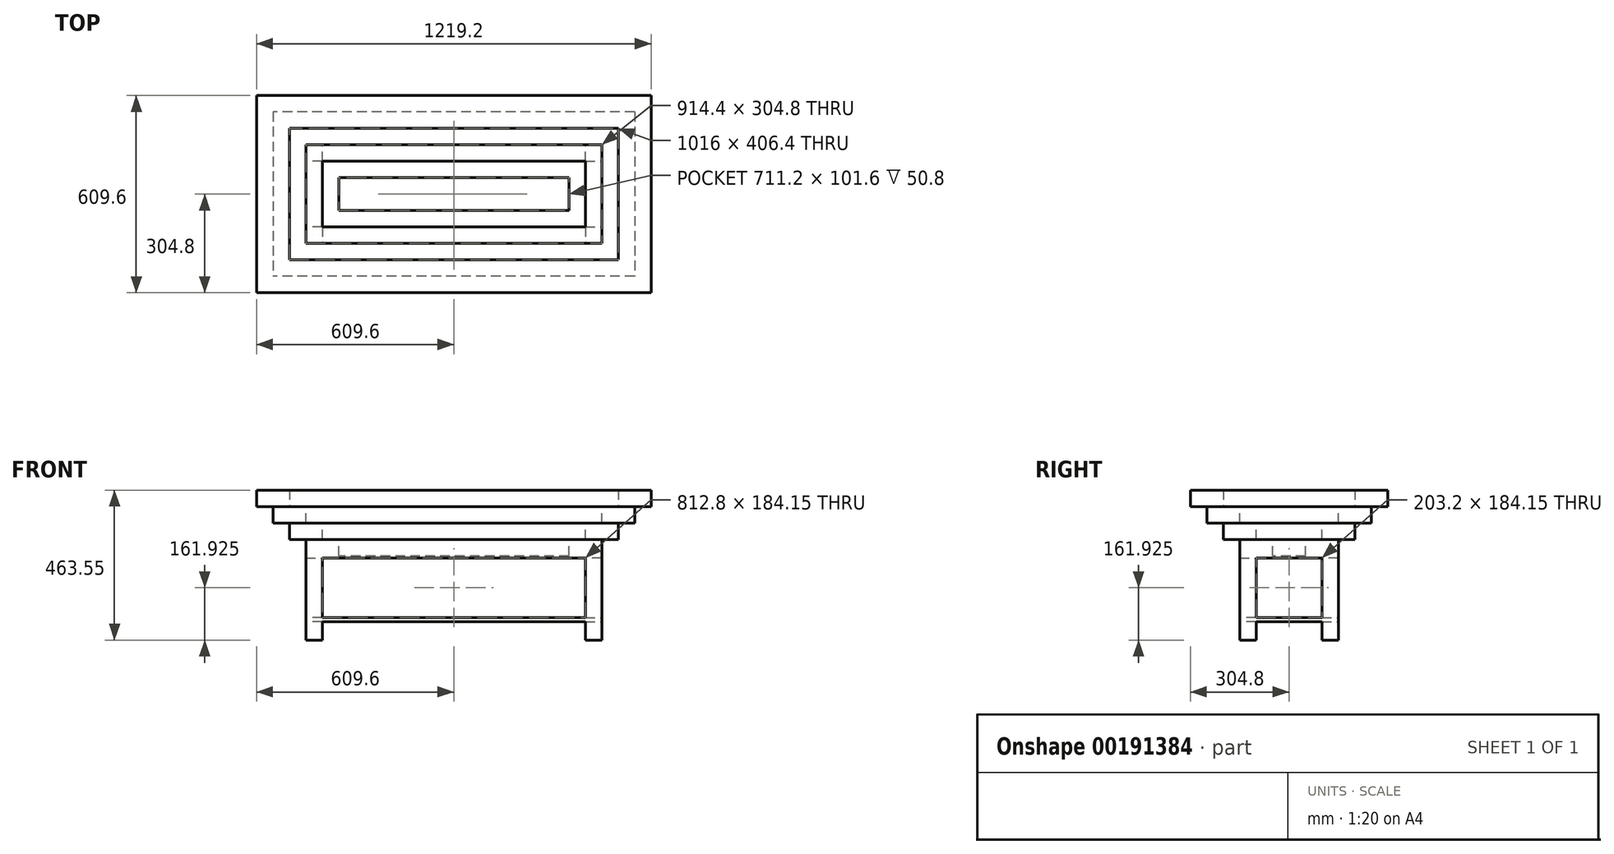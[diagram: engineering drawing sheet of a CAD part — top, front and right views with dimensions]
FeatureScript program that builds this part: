
annotation { "Feature Type Name" : "Feature", "Feature Type Description" : "" }
export const myFeature = defineFeature(function(context is Context, id is Id, definition is map)
    precondition{}
    {
        {
            var Q0;
            Q0=qCreatedBy(makeId("Top.planeOp"),FACE);
            var sketch = newSketch(context, id + "F0", { "sketchPlane" : qUnion([Q0])});
            skLineSegment(sketch, "E0.bottom", {"start": v(609.6, -304.8) * mm, "end": v(-609.6, -304.8) * mm});
            skLineSegment(sketch, "E0.top", {"start": v(609.6, 304.8) * mm, "end": v(-609.6, 304.8) * mm});
            skLineSegment(sketch, "E0.left", {"start": v(609.6, -304.8) * mm, "end": v(609.6, 304.8) * mm});
            skLineSegment(sketch, "E0.right", {"start": v(-609.6, -304.8) * mm, "end": v(-609.6, 304.8) * mm});
            skPoint(sketch, "E0.middle", {"position": v(0, 0) * mm});
            skLineSegment(sketch, "E1.0", {"start": v(508, 203.2) * mm, "end": v(-508, 203.2) * mm});
            skLineSegment(sketch, "E1.1", {"start": v(508, -203.2) * mm, "end": v(508, 203.2) * mm});
            skLineSegment(sketch, "E1.2", {"start": v(508, -203.2) * mm, "end": v(-508, -203.2) * mm});
            skLineSegment(sketch, "E1.3", {"start": v(-508, -203.2) * mm, "end": v(-508, 203.2) * mm});
            skSolve(sketch);
        }
        {
            var Q0;
            Q0 = qSketchRegion(id + "F0", true);
            extrude(context, id + "F1", {"entities" : qUnion([Q0]), "depth" : 50.8 * mm});
        }
        {
            var Q0;
            Q0=makeQuery(id+"F1.opExtrude","CAP_FACE",FACE,{"disambiguationData":[OSD([sQuery(id+"F0.wireOp",EDGE,"E0.bottom"),sQuery(id+"F0.wireOp",EDGE,"E0.top"),sQuery(id+"F0.wireOp",EDGE,"E0.left"),sQuery(id+"F0.wireOp",EDGE,"E0.right"),sQuery(id+"F0.wireOp",EDGE,"E1.0"),sQuery(id+"F0.wireOp",EDGE,"E1.1"),sQuery(id+"F0.wireOp",EDGE,"E1.2"),sQuery(id+"F0.wireOp",EDGE,"E1.3")])],"isStart":true});
            var sketch = newSketch(context, id + "F2", { "sketchPlane" : qUnion([Q0])});
            skLineSegment(sketch, "E2.bottom", {"start": v(558.8, -254) * mm, "end": v(-558.8, -254) * mm});
            skLineSegment(sketch, "E2.top", {"start": v(558.8, 254) * mm, "end": v(-558.8, 254) * mm});
            skLineSegment(sketch, "E2.left", {"start": v(558.8, -254) * mm, "end": v(558.8, 254) * mm});
            skLineSegment(sketch, "E2.right", {"start": v(-558.8, -254) * mm, "end": v(-558.8, 254) * mm});
            skPoint(sketch, "E2.middle", {"position": v(0, 0) * mm});
            skLineSegment(sketch, "E3.0", {"start": v(457.2, 152.4) * mm, "end": v(-457.2, 152.4) * mm});
            skLineSegment(sketch, "E3.1", {"start": v(457.2, -152.4) * mm, "end": v(457.2, 152.4) * mm});
            skLineSegment(sketch, "E3.2", {"start": v(457.2, -152.4) * mm, "end": v(-457.2, -152.4) * mm});
            skLineSegment(sketch, "E3.3", {"start": v(-457.2, -152.4) * mm, "end": v(-457.2, 152.4) * mm});
            skSolve(sketch);
        }
        {
            var Q0;
            Q0 = qSketchRegion(id + "F2", true);
            extrude(context, id + "F3", {"entities" : qUnion([Q0]), "operationType" : NewBodyOperationType.ADD, "depth" : 50.8 * mm});
        }
        {
            var Q0;
            Q0=makeQuery(id+"F3.opExtrude","CAP_FACE",FACE,{"disambiguationData":[OSD([sQuery(id+"F2.wireOp",EDGE,"E2.bottom"),sQuery(id+"F2.wireOp",EDGE,"E2.top"),sQuery(id+"F2.wireOp",EDGE,"E2.left"),sQuery(id+"F2.wireOp",EDGE,"E2.right"),sQuery(id+"F2.wireOp",EDGE,"E3.0"),sQuery(id+"F2.wireOp",EDGE,"E3.1"),sQuery(id+"F2.wireOp",EDGE,"E3.2"),sQuery(id+"F2.wireOp",EDGE,"E3.3")])],"isStart":false});
            var sketch = newSketch(context, id + "F4", { "sketchPlane" : qUnion([Q0])});
            skLineSegment(sketch, "E4.bottom", {"start": v(508, -203.2) * mm, "end": v(-508, -203.2) * mm});
            skLineSegment(sketch, "E4.top", {"start": v(508, 203.2) * mm, "end": v(-508, 203.2) * mm});
            skLineSegment(sketch, "E4.left", {"start": v(508, -203.2) * mm, "end": v(508, 203.2) * mm});
            skLineSegment(sketch, "E4.right", {"start": v(-508, -203.2) * mm, "end": v(-508, 203.2) * mm});
            skPoint(sketch, "E4.middle", {"position": v(0, 0) * mm});
            skLineSegment(sketch, "E5.0", {"start": v(406.4, 101.6) * mm, "end": v(-406.4, 101.6) * mm});
            skLineSegment(sketch, "E5.1", {"start": v(406.4, -101.6) * mm, "end": v(406.4, 101.6) * mm});
            skLineSegment(sketch, "E5.2", {"start": v(406.4, -101.6) * mm, "end": v(-406.4, -101.6) * mm});
            skLineSegment(sketch, "E5.3", {"start": v(-406.4, -101.6) * mm, "end": v(-406.4, 101.6) * mm});
            skSolve(sketch);
        }
        {
            var Q0;
            Q0 = qSketchRegion(id + "F4", true);
            extrude(context, id + "F5", {"entities" : qUnion([Q0]), "operationType" : NewBodyOperationType.ADD, "depth" : 50.8 * mm});
        }
        {
            var Q0;
            Q0=makeQuery(id+"F5.opExtrude","CAP_FACE",FACE,{"disambiguationData":[OSD([sQuery(id+"F4.wireOp",EDGE,"E4.bottom"),sQuery(id+"F4.wireOp",EDGE,"E4.top"),sQuery(id+"F4.wireOp",EDGE,"E4.left"),sQuery(id+"F4.wireOp",EDGE,"E4.right"),sQuery(id+"F4.wireOp",EDGE,"E5.0"),sQuery(id+"F4.wireOp",EDGE,"E5.1"),sQuery(id+"F4.wireOp",EDGE,"E5.2"),sQuery(id+"F4.wireOp",EDGE,"E5.3")])],"isStart":false});
            var sketch = newSketch(context, id + "F6", { "sketchPlane" : qUnion([Q0])});
            skLineSegment(sketch, "E6.bottom", {"start": v(457.2, -152.4) * mm, "end": v(-457.2, -152.4) * mm});
            skLineSegment(sketch, "E6.top", {"start": v(457.2, 152.4) * mm, "end": v(-457.2, 152.4) * mm});
            skLineSegment(sketch, "E6.left", {"start": v(457.2, -152.4) * mm, "end": v(457.2, 152.4) * mm});
            skLineSegment(sketch, "E6.right", {"start": v(-457.2, -152.4) * mm, "end": v(-457.2, 152.4) * mm});
            skPoint(sketch, "E6.middle", {"position": v(0, 0) * mm});
            skLineSegment(sketch, "E7.0", {"start": v(355.6, 50.8) * mm, "end": v(-355.6, 50.8) * mm});
            skLineSegment(sketch, "E7.1", {"start": v(355.6, -50.8) * mm, "end": v(355.6, 50.8) * mm});
            skLineSegment(sketch, "E7.2", {"start": v(355.6, -50.8) * mm, "end": v(-355.6, -50.8) * mm});
            skLineSegment(sketch, "E7.3", {"start": v(-355.6, -50.8) * mm, "end": v(-355.6, 50.8) * mm});
            skSolve(sketch);
        }
        {
            var Q0;
            Q0 = qSketchRegion(id + "F6", true);
            extrude(context, id + "F7", {"entities" : qUnion([Q0]), "operationType" : NewBodyOperationType.ADD, "depth" : 50.8 * mm});
        }
        {
            var Q0;
            Q0=makeQuery(id+"F7.opExtrude","CAP_FACE",FACE,{"disambiguationData":[OSD([sQuery(id+"F6.wireOp",EDGE,"E6.bottom"),sQuery(id+"F6.wireOp",EDGE,"E6.top"),sQuery(id+"F6.wireOp",EDGE,"E6.left"),sQuery(id+"F6.wireOp",EDGE,"E6.right"),sQuery(id+"F6.wireOp",EDGE,"E7.0"),sQuery(id+"F6.wireOp",EDGE,"E7.1"),sQuery(id+"F6.wireOp",EDGE,"E7.2"),sQuery(id+"F6.wireOp",EDGE,"E7.3")])],"isStart":false});
            var sketch = newSketch(context, id + "F8", { "sketchPlane" : qUnion([Q0])});
            skLineSegment(sketch, "E8.bottom", {"start": v(457.2, -152.4) * mm, "end": v(-457.2, -152.4) * mm});
            skLineSegment(sketch, "E8.top", {"start": v(457.2, 152.4) * mm, "end": v(-457.2, 152.4) * mm});
            skLineSegment(sketch, "E8.left", {"start": v(457.2, -152.4) * mm, "end": v(457.2, 152.4) * mm});
            skLineSegment(sketch, "E8.right", {"start": v(-457.2, -152.4) * mm, "end": v(-457.2, 152.4) * mm});
            skPoint(sketch, "E8.middle", {"position": v(0, 0) * mm});
            skSolve(sketch);
        }
        {
            var Q0;
            Q0 = qSketchRegion(id + "F8", true);
            extrude(context, id + "F9", {"entities" : qUnion([Q0]), "operationType" : NewBodyOperationType.ADD, "depth" : 6.35 * mm});
        }
        {
            var Q0;
            Q0=makeQuery(id+"F9.opExtrude","CAP_FACE",FACE,{"disambiguationData":[OSD([sQuery(id+"F8.wireOp",EDGE,"E8.bottom"),sQuery(id+"F8.wireOp",EDGE,"E8.top"),sQuery(id+"F8.wireOp",EDGE,"E8.left"),sQuery(id+"F8.wireOp",EDGE,"E8.right")])],"isStart":false});
            var sketch = newSketch(context, id + "F10", { "sketchPlane" : qUnion([Q0])});
            skLineSegment(sketch, "E9", {"start": v(0, 152.4) * mm, "end": v(0, -152.4) * mm});
            skLineSegment(sketch, "E10.bottom", {"start": v(-457.2, 152.4) * mm, "end": v(-406.4, 152.4) * mm});
            skLineSegment(sketch, "E10.top", {"start": v(-457.2, 101.6) * mm, "end": v(-406.4, 101.6) * mm});
            skLineSegment(sketch, "E10.left", {"start": v(-457.2, 152.4) * mm, "end": v(-457.2, 101.6) * mm});
            skLineSegment(sketch, "E10.right", {"start": v(-406.4, 152.4) * mm, "end": v(-406.4, 101.6) * mm});
            skLineSegment(sketch, "E11.bottom", {"start": v(-457.2, -152.4) * mm, "end": v(-406.4, -152.4) * mm});
            skLineSegment(sketch, "E11.top", {"start": v(-457.2, -101.6) * mm, "end": v(-406.4, -101.6) * mm});
            skLineSegment(sketch, "E11.left", {"start": v(-457.2, -152.4) * mm, "end": v(-457.2, -101.6) * mm});
            skLineSegment(sketch, "E11.right", {"start": v(-406.4, -152.4) * mm, "end": v(-406.4, -101.6) * mm});
            skLineSegment(sketch, "E12.MirrorCS", {"start": v(406.4, 152.4) * mm, "end": v(406.4, 101.6) * mm});
            skLineSegment(sketch, "E13.MirrorCS", {"start": v(457.2, 101.6) * mm, "end": v(406.4, 101.6) * mm});
            skLineSegment(sketch, "E14.MirrorCS", {"start": v(457.2, 152.4) * mm, "end": v(457.2, 101.6) * mm});
            skLineSegment(sketch, "E15.MirrorCS", {"start": v(457.2, 152.4) * mm, "end": v(406.4, 152.4) * mm});
            skLineSegment(sketch, "E16.MirrorCS", {"start": v(457.2, -101.6) * mm, "end": v(406.4, -101.6) * mm});
            skLineSegment(sketch, "E17.MirrorCS", {"start": v(457.2, -152.4) * mm, "end": v(457.2, -101.6) * mm});
            skLineSegment(sketch, "E18.MirrorCS", {"start": v(457.2, -152.4) * mm, "end": v(406.4, -152.4) * mm});
            skLineSegment(sketch, "E19.MirrorCS", {"start": v(406.4, -152.4) * mm, "end": v(406.4, -101.6) * mm});
            skSolve(sketch);
        }
        {
            var Q0;
            Q0=makeQuery(id+"F10.imprint","IMPRINT",FACE,{"disambiguationData":[TD([[makeQuery(id+"F10.imprint","IMPRINT",EDGE,{"derivedFrom":sQuery(id+"F10.wireOp",EDGE,"E10.bottom")}),1.0]])]});
            var Q1;
            Q1=makeQuery(id+"F10.imprint","IMPRINT",FACE,{"disambiguationData":[TD([[makeQuery(id+"F10.imprint","IMPRINT",EDGE,{"derivedFrom":sQuery(id+"F10.wireOp",EDGE,"E11.bottom")}),-1.0]])]});
            var Q2;
            Q2=makeQuery(id+"F10.imprint","IMPRINT",FACE,{"disambiguationData":[TD([[makeQuery(id+"F10.imprint","IMPRINT",EDGE,{"derivedFrom":sQuery(id+"F10.wireOp",EDGE,"E12.MirrorCS")}),1.0]])]});
            var Q3;
            Q3=makeQuery(id+"F10.imprint","IMPRINT",FACE,{"disambiguationData":[TD([[makeQuery(id+"F10.imprint","IMPRINT",EDGE,{"derivedFrom":sQuery(id+"F10.wireOp",EDGE,"E16.MirrorCS")}),1.0]])]});
            extrude(context, id + "F11", {"entities" : qUnion([Q0, Q1, Q2, Q3]), "operationType" : NewBodyOperationType.ADD, "depth" : 254 * mm});
        }
        {
            var Q0;
            Q0=makeQuery(id+"F1.opExtrude","CAP_FACE",FACE,{"disambiguationData":[OSD([sQuery(id+"F0.wireOp",EDGE,"E0.bottom"),sQuery(id+"F0.wireOp",EDGE,"E0.top"),sQuery(id+"F0.wireOp",EDGE,"E0.left"),sQuery(id+"F0.wireOp",EDGE,"E0.right"),sQuery(id+"F0.wireOp",EDGE,"E1.0"),sQuery(id+"F0.wireOp",EDGE,"E1.1"),sQuery(id+"F0.wireOp",EDGE,"E1.2"),sQuery(id+"F0.wireOp",EDGE,"E1.3")])],"isStart":false});
            cPlane(context, id + "F12", {"entities" : qUnion([Q0]), "cplaneType" : CPlaneType.OFFSET, "offset" : 406.4 * mm, "oppositeDirection" : true, "width" : 152.4 * mm, "height" : 152.4 * mm});
        }
        {
            var Q0;
            Q0=qCreatedBy(id+"F12.planeOp",FACE);
            var sketch = newSketch(context, id + "F13", { "sketchPlane" : qUnion([Q0])});
            skLineSegment(sketch, "E20.bottom", {"start": v(457.2, 152.4) * mm, "end": v(-457.2, 152.4) * mm});
            skLineSegment(sketch, "E20.top", {"start": v(457.2, -152.4) * mm, "end": v(-457.2, -152.4) * mm});
            skLineSegment(sketch, "E20.left", {"start": v(457.2, 152.4) * mm, "end": v(457.2, -152.4) * mm});
            skLineSegment(sketch, "E20.right", {"start": v(-457.2, 152.4) * mm, "end": v(-457.2, -152.4) * mm});
            skPoint(sketch, "E20.middle", {"position": v(0, 0) * mm});
            skSolve(sketch);
        }
        {
            var Q0;
            Q0 = qSketchRegion(id + "F13", true);
            extrude(context, id + "F14", {"entities" : qUnion([Q0]), "operationType" : NewBodyOperationType.ADD, "depth" : 12.7 * mm});
        }
    });
